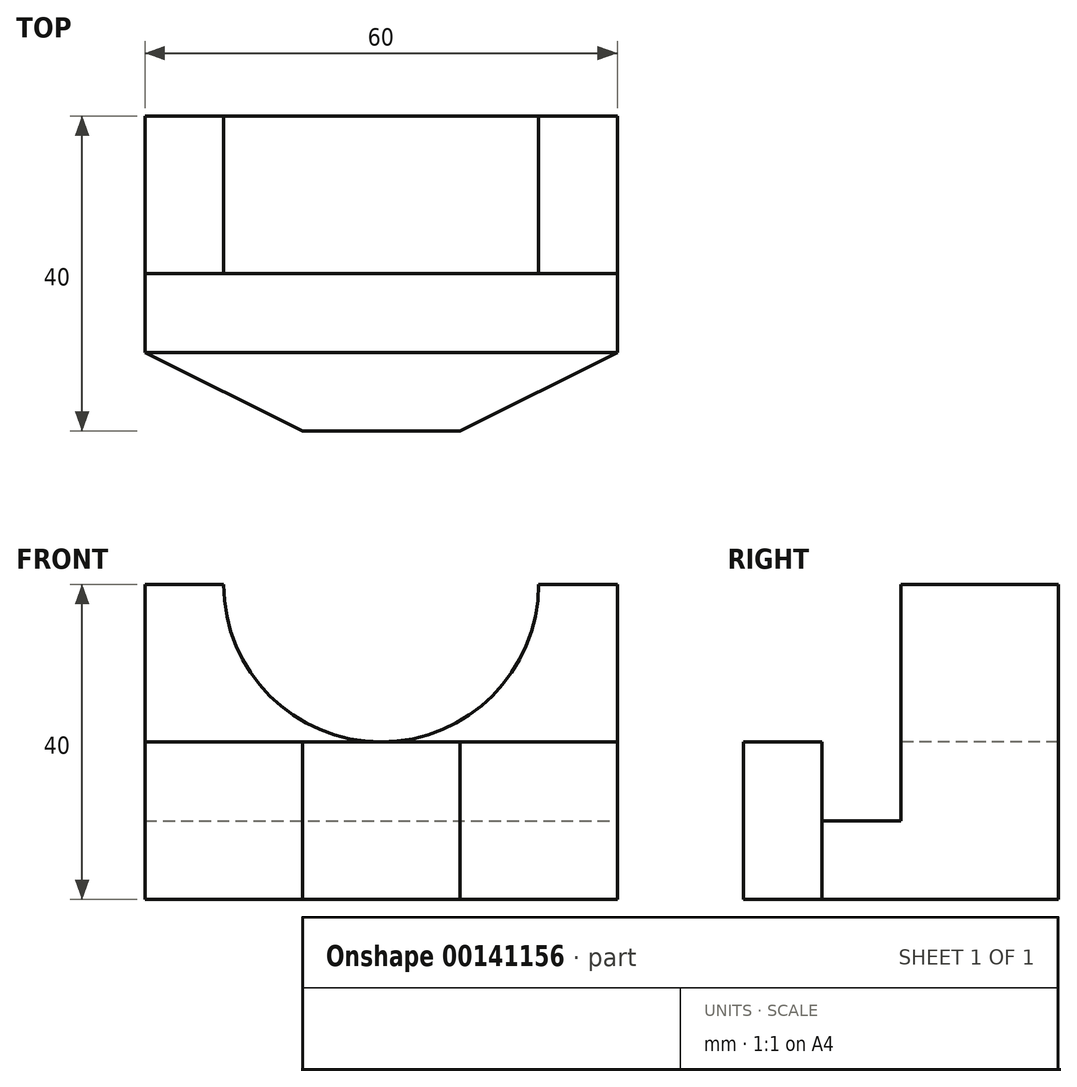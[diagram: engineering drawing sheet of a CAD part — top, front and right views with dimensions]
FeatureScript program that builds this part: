
annotation { "Feature Type Name" : "Feature", "Feature Type Description" : "" }
export const myFeature = defineFeature(function(context is Context, id is Id, definition is map)
    precondition{}
    {
        {
            var Q0;
            Q0=qCreatedBy(makeId("Top.planeOp"),FACE);
            var sketch = newSketch(context, id + "F0", { "sketchPlane" : qUnion([Q0])});
            skLineSegment(sketch, "E0.bottom", {"start": v(0, 0) * mm, "end": v(60, 0) * mm});
            skLineSegment(sketch, "E0.top", {"start": v(0, 40) * mm, "end": v(60, 40) * mm});
            skLineSegment(sketch, "E0.left", {"start": v(0, 0) * mm, "end": v(0, 40) * mm});
            skLineSegment(sketch, "E0.right", {"start": v(60, 0) * mm, "end": v(60, 40) * mm});
            skLineSegment(sketch, "E1", {"start": v(60, 10) * mm, "end": v(40, 0) * mm});
            skLineSegment(sketch, "E2", {"start": v(0, 10) * mm, "end": v(20, 0) * mm});
            skSolve(sketch);
        }
        {
            var Q0;
            {var subQ1=sQuery(id+"F0.wireOp",EDGE,"E0.top");Q0=makeQuery(id+"F0.imprint","IMPRINT",FACE,{"disambiguationData":[TD([[makeQuery(id+"F0.imprint","IMPRINT",EDGE,{"derivedFrom":subQ1}),-1.0]])]});}
            extrude(context, id + "F1", {"entities" : qUnion([Q0]), "depth" : 40 * mm});
        }
        {
            var Q0;
            Q0=makeQuery(id+"F1.opExtrude","SWEPT_FACE",FACE,{"disambiguationData":[OSD([sQuery(id+"F0.wireOp",EDGE,"E0.right")])]});
            var sketch = newSketch(context, id + "F2", { "sketchPlane" : qUnion([Q0])});
            skLineSegment(sketch, "E3.bottom", {"start": v(10, 40) * mm, "end": v(20, 40) * mm});
            skLineSegment(sketch, "E3.top", {"start": v(10, 10) * mm, "end": v(20, 10) * mm});
            skLineSegment(sketch, "E3.left", {"start": v(10, 40) * mm, "end": v(10, 10) * mm});
            skLineSegment(sketch, "E3.right", {"start": v(20, 40) * mm, "end": v(20, 10) * mm});
            skSolve(sketch);
        }
        {
            var Q0;
            Q0 = qSketchRegion(id + "F2", true);
            extrude(context, id + "F3", {"entities" : qUnion([Q0]), "operationType" : NewBodyOperationType.REMOVE, "endBound" : BoundingType.THROUGH_ALL, "oppositeDirection" : true, "depth" : 25 * mm});
        }
        {
            var Q0;
            Q0=makeQuery(id+"F1.opExtrude","SWEPT_FACE",FACE,{"disambiguationData":[OSD([sQuery(id+"F0.wireOp",EDGE,"E0.bottom")])]});
            var sketch = newSketch(context, id + "F4", { "sketchPlane" : qUnion([Q0])});
            skLineSegment(sketch, "E4.bottom", {"start": v(0, 40) * mm, "end": v(60, 40) * mm});
            skLineSegment(sketch, "E4.top", {"start": v(0, 20) * mm, "end": v(60, 20) * mm});
            skLineSegment(sketch, "E4.left", {"start": v(0, 40) * mm, "end": v(0, 20) * mm});
            skLineSegment(sketch, "E4.right", {"start": v(60, 40) * mm, "end": v(60, 20) * mm});
            skSolve(sketch);
        }
        {
            var Q0;
            Q0 = qSketchRegion(id + "F4", true);
            extrude(context, id + "F5", {"entities" : qUnion([Q0]), "operationType" : NewBodyOperationType.REMOVE, "oppositeDirection" : true, "depth" : 10 * mm});
        }
        {
            var Q0;
            Q0=makeQuery(id+"F3.boolean.opBoolean","COPY",FACE,{"derivedFrom":makeQuery(id+"F3.opExtrude","SWEPT_FACE",FACE,{"disambiguationData":[OSD([sQuery(id+"F2.wireOp",EDGE,"E3.right")])]})});
            var sketch = newSketch(context, id + "F6", { "sketchPlane" : qUnion([Q0])});
            skArc(sketch, "E5", {"start": v(10, 40) * mm, "mid": v(30, 20) * mm, "end": v(50, 40) * mm});
            skLineSegment(sketch, "E6", {"start": v(10, 40) * mm, "end": v(50, 40) * mm});
            skSolve(sketch);
        }
        {
            var Q0;
            Q0=makeQuery(id+"F6.imprint","IMPRINT",FACE,{"disambiguationData":[TD([[makeQuery(id+"F6.imprint","IMPRINT",EDGE,{"derivedFrom":sQuery(id+"F6.wireOp",EDGE,"E5")}),1.0]])]});
            extrude(context, id + "F7", {"entities" : qUnion([Q0]), "operationType" : NewBodyOperationType.REMOVE, "endBound" : BoundingType.THROUGH_ALL, "oppositeDirection" : true, "depth" : 25 * mm});
        }
    });
